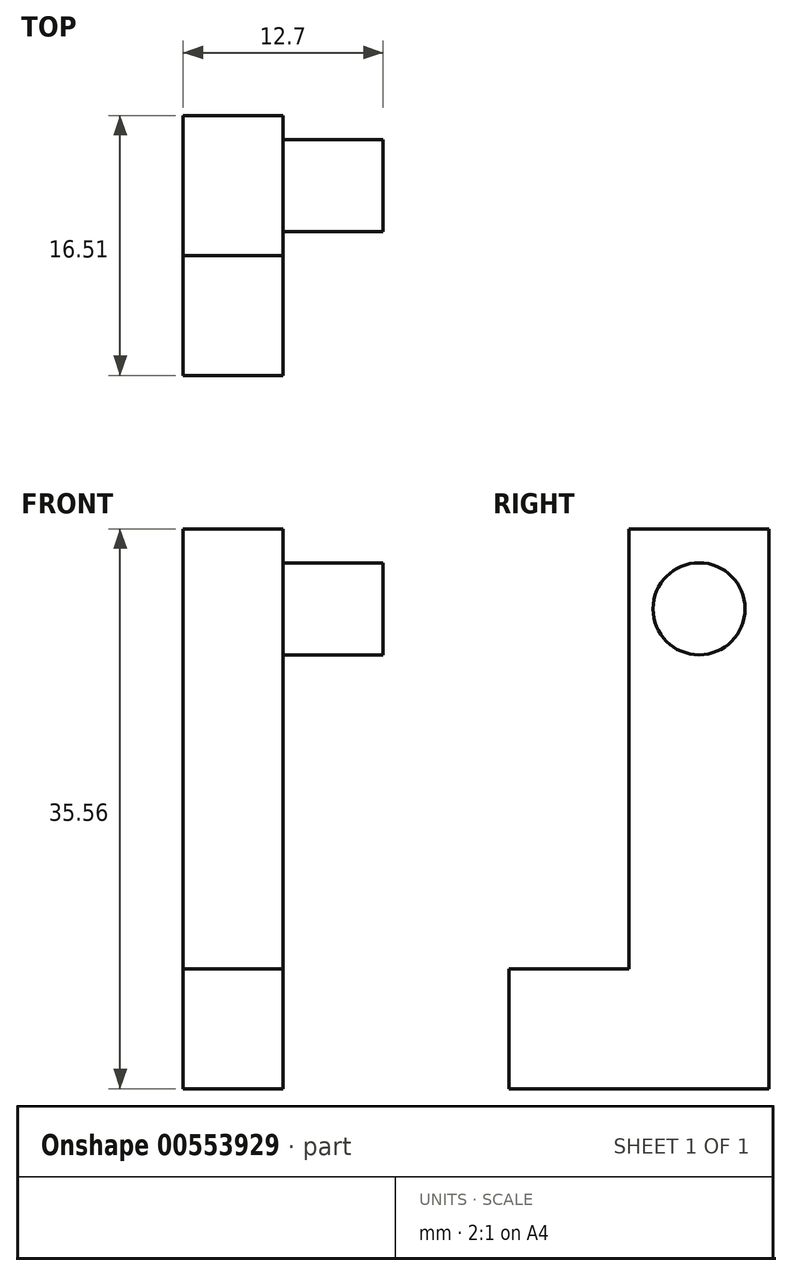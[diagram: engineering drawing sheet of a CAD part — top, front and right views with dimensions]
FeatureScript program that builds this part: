
annotation { "Feature Type Name" : "Feature", "Feature Type Description" : "" }
export const myFeature = defineFeature(function(context is Context, id is Id, definition is map)
    precondition{}
    {
        {
            var Q0;
            Q0=qCreatedBy(makeId("Right.planeOp"),FACE);
            var sketch = newSketch(context, id + "F0", { "sketchPlane" : qUnion([Q0])});
            skLineSegment(sketch, "E0.left", {"start": v(0, 0) * mm, "end": v(0, 35.56) * mm});
            skLineSegment(sketch, "E1", {"start": v(0, 35.56) * mm, "end": v(-8.9, 35.56) * mm});
            skLineSegment(sketch, "E2", {"start": v(-8.9, 35.56) * mm, "end": v(-8.89, 7.62) * mm});
            skLineSegment(sketch, "E3", {"start": v(-8.89, 7.62) * mm, "end": v(-16.51, 7.62) * mm});
            skLineSegment(sketch, "E4", {"start": v(-16.51, 7.62) * mm, "end": v(-16.51, 0) * mm});
            skLineSegment(sketch, "E5", {"start": v(-16.51, 0) * mm, "end": v(0, 0) * mm});
            skSolve(sketch);
        }
        {
            var Q0;
            Q0=makeQuery(id+"F0.imprint","IMPRINT",FACE,{"disambiguationData":[TD([[makeQuery(id+"F0.imprint","IMPRINT",EDGE,{"derivedFrom":sQuery(id+"F0.wireOp",EDGE,"E0.left")}),1.0]])]});
            extrude(context, id + "F1", {"entities" : qUnion([Q0]), "depth" : 6.35 * mm, "offsetDistance" : 25.4 * mm});
        }
        {
            var Q0;
            Q0=makeQuery(id+"F1.opExtrude","CAP_FACE",FACE,{"disambiguationData":[OSD([sQuery(id+"F0.wireOp",EDGE,"E0.left"),sQuery(id+"F0.wireOp",EDGE,"E1"),sQuery(id+"F0.wireOp",EDGE,"E2"),sQuery(id+"F0.wireOp",EDGE,"E3"),sQuery(id+"F0.wireOp",EDGE,"E4"),sQuery(id+"F0.wireOp",EDGE,"E5")])],"isStart":false});
            var sketch = newSketch(context, id + "F2", { "sketchPlane" : qUnion([Q0])});
            skCircle(sketch, "E6", {"center": v(-4.45, 30.48) * mm, "radius": 2.92 * mm});
            skSolve(sketch);
        }
        {
            var Q0;
            Q0=makeQuery(id+"F2.imprint","IMPRINT",FACE,{"disambiguationData":[TD([[makeQuery(id+"F2.imprint","IMPRINT",EDGE,{"derivedFrom":sQuery(id+"F2.wireOp",EDGE,"E6")}),1.0]])]});
            extrude(context, id + "F3", {"entities" : qUnion([Q0]), "operationType" : NewBodyOperationType.ADD, "depth" : 6.35 * mm, "offsetDistance" : 25.4 * mm});
        }
    });
